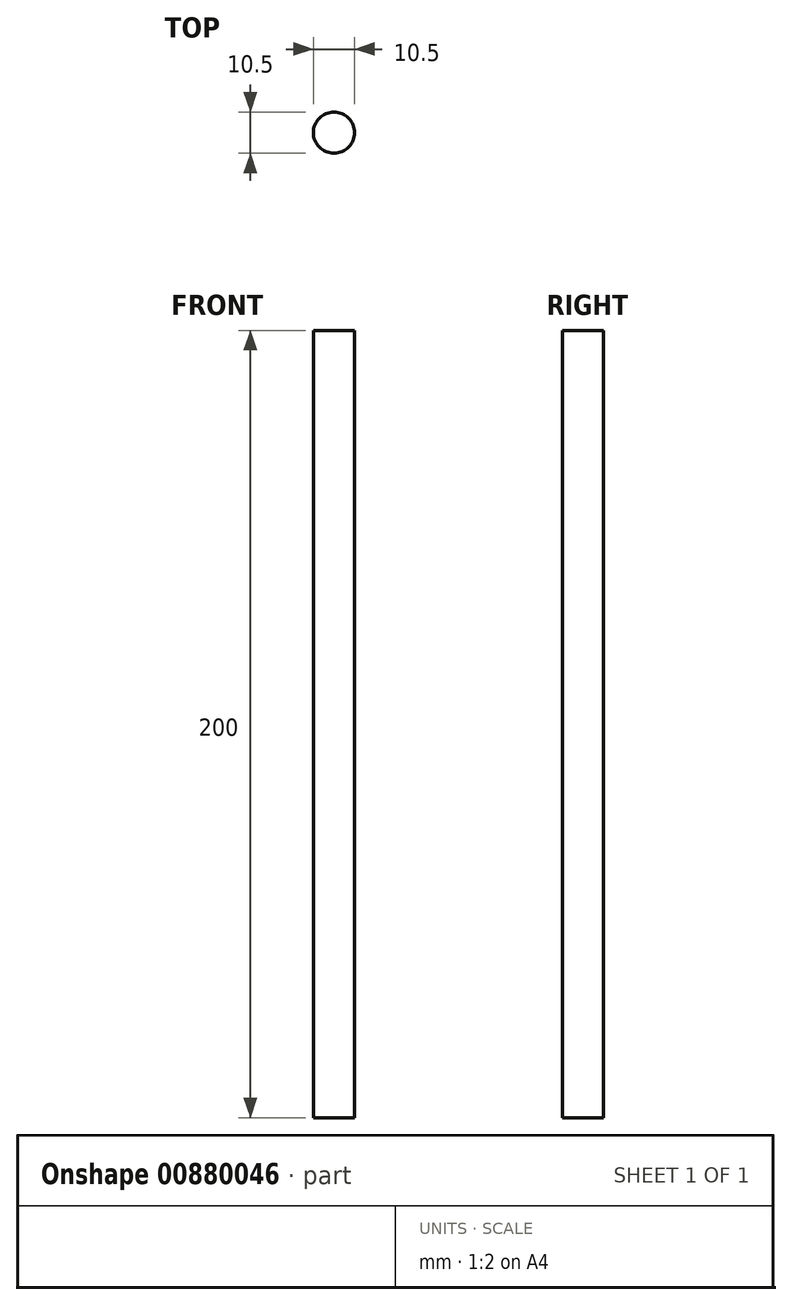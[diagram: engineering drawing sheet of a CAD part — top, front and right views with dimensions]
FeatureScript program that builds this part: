
annotation { "Feature Type Name" : "Feature", "Feature Type Description" : "" }
export const myFeature = defineFeature(function(context is Context, id is Id, definition is map)
    precondition{}
    {
        {
            var Q0;
            Q0=qCreatedBy(makeId("Top.planeOp"),FACE);
            var sketch = newSketch(context, id + "F0", { "sketchPlane" : qUnion([Q0])});
            skCircle(sketch, "E0", {"center": v(0, 0) * mm, "radius": 5.25 * mm});
            skSolve(sketch);
        }
        {
            var Q0;
            Q0=qSketchRegion(id+"F0",true);
            extrude(context, id + "F1", {"entities" : qUnion([Q0]), "endBound" : BoundingType.SYMMETRIC, "depth" : 200 * mm});
        }
    });
